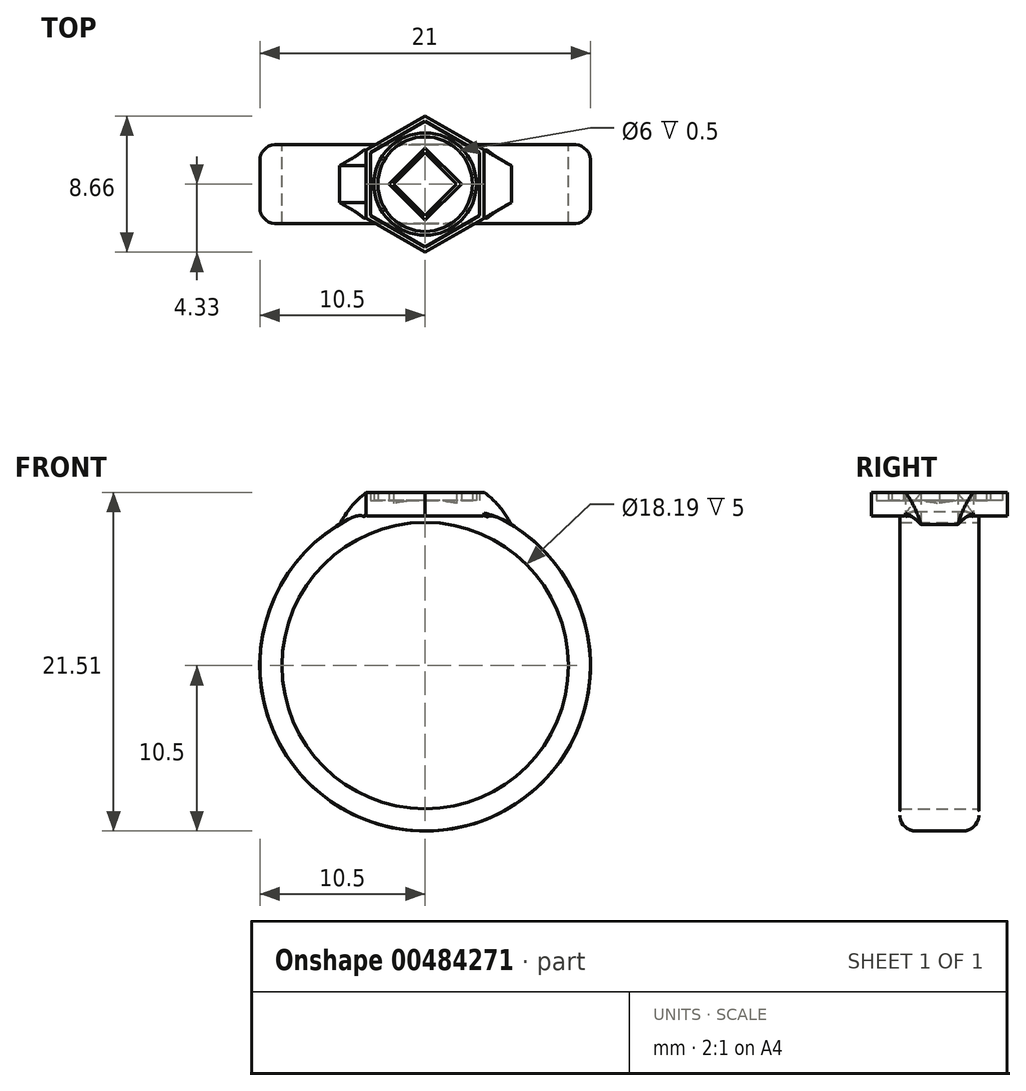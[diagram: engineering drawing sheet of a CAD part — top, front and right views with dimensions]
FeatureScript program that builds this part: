
annotation { "Feature Type Name" : "Feature", "Feature Type Description" : "" }
export const myFeature = defineFeature(function(context is Context, id is Id, definition is map)
    precondition{}
    {
        {
            var Q0;
            Q0=qCreatedBy(makeId("Front.planeOp"),FACE);
            var sketch = newSketch(context, id + "F0", { "sketchPlane" : qUnion([Q0])});
            skCircle(sketch, "E0", {"center": v(0, 0) * mm, "radius": 9.1 * mm});
            skCircle(sketch, "E1", {"center": v(0, 0) * mm, "radius": 10.5 * mm});
            skSolve(sketch);
        }
        {
            var Q0;
            Q0=makeQuery(id+"F0.imprint","IMPRINT",FACE,{"disambiguationData":[TD([[makeQuery(id+"F0.imprint","IMPRINT",EDGE,{"derivedFrom":sQuery(id+"F0.wireOp",EDGE,"E0")}),-1.0]])]});
            extrude(context, id + "F1", {"entities" : qUnion([Q0]), "endBound" : BoundingType.SYMMETRIC, "depth" : 5 * mm});
        }
        {
            var Q0;
            Q0=qCreatedBy(makeId("Top.planeOp"),FACE);
            var sketch = newSketch(context, id + "F2", { "sketchPlane" : qUnion([Q0])});
            skLineSegment(sketch, "E2.0", {"start": v(0, 4) * mm, "end": v(3.46, 2) * mm});
            skLineSegment(sketch, "E2.1", {"start": v(3.46, 2) * mm, "end": v(3.46, -2) * mm});
            skLineSegment(sketch, "E2.2", {"start": v(3.46, -2) * mm, "end": v(0, -4) * mm});
            skLineSegment(sketch, "E2.3", {"start": v(0, -4) * mm, "end": v(-3.46, -2) * mm});
            skLineSegment(sketch, "E2.4", {"start": v(-3.46, -2) * mm, "end": v(-3.46, 2) * mm});
            skLineSegment(sketch, "E2.5", {"start": v(-3.46, 2) * mm, "end": v(0, 4) * mm});
            skCircle(sketch, "E3", {"center": v(0, 0) * mm, "radius": 3.25 * mm});
            skCircle(sketch, "E4.cCircle", {"center": v(0, 0) * mm, "radius": 3.25 * mm, "construction": true});
            skLineSegment(sketch, "E5.0", {"start": v(0, 2.3) * mm, "end": v(2.3, 0) * mm});
            skLineSegment(sketch, "E5.1", {"start": v(2.3, 0) * mm, "end": v(0, -2.3) * mm});
            skLineSegment(sketch, "E5.2", {"start": v(0, -2.3) * mm, "end": v(-2.3, 0) * mm});
            skLineSegment(sketch, "E5.3", {"start": v(-2.3, 0) * mm, "end": v(0, 2.3) * mm});
            skCircle(sketch, "E6", {"center": v(0, 0) * mm, "radius": 3 * mm});
            skPoint(sketch, "E7.cCircle.perimeterSnap0", {"position": v(3.46, 0) * mm});
            skLineSegment(sketch, "E7.0", {"start": v(3.75, 2.17) * mm, "end": v(3.75, -2.17) * mm});
            skLineSegment(sketch, "E7.1", {"start": v(3.75, -2.17) * mm, "end": v(0, -4.33) * mm});
            skLineSegment(sketch, "E7.2", {"start": v(0, -4.33) * mm, "end": v(-3.75, -2.17) * mm});
            skLineSegment(sketch, "E7.3", {"start": v(-3.75, -2.17) * mm, "end": v(-3.75, 2.17) * mm});
            skLineSegment(sketch, "E7.4", {"start": v(-3.75, 2.17) * mm, "end": v(0, 4.33) * mm});
            skLineSegment(sketch, "E7.5", {"start": v(0, 4.33) * mm, "end": v(3.75, 2.17) * mm});
            skPoint(sketch, "E7.0.midPoint", {"position": v(3.75, 0) * mm});
            skPoint(sketch, "E7.0.midPoint.positionSnap0", {"position": v(3.46, 0) * mm});
            skLineSegment(sketch, "E8.0", {"start": v(-2, 0) * mm, "end": v(0, 2) * mm});
            skLineSegment(sketch, "E8.1", {"start": v(0, 2) * mm, "end": v(2, 0) * mm});
            skLineSegment(sketch, "E8.2", {"start": v(2, 0) * mm, "end": v(0, -2) * mm});
            skLineSegment(sketch, "E8.3", {"start": v(0, -2) * mm, "end": v(-2, 0) * mm});
            skSolve(sketch);
        }
        {
            var Q0;
            Q0=makeQuery(id+"F2.imprint","IMPRINT",FACE,{"disambiguationData":[TD([[makeQuery(id+"F2.imprint","IMPRINT",EDGE,{"derivedFrom":sQuery(id+"F2.wireOp",EDGE,"E5.0")}),-1.0]])]});
            var Q1;
            Q1=makeQuery(id+"F2.imprint","IMPRINT",FACE,{"disambiguationData":[TD([[makeQuery(id+"F2.imprint","IMPRINT",EDGE,{"derivedFrom":sQuery(id+"F2.wireOp",EDGE,"E5.0")}),1.0]])]});
            var Q2;
            Q2=makeQuery(id+"F2.imprint","IMPRINT",FACE,{"disambiguationData":[TD([[makeQuery(id+"F2.imprint","IMPRINT",EDGE,{"derivedFrom":sQuery(id+"F2.wireOp",EDGE,"E3")}),1.0]])]});
            var Q3;
            Q3=makeQuery(id+"F2.imprint","IMPRINT",FACE,{"disambiguationData":[TD([[makeQuery(id+"F2.imprint","IMPRINT",EDGE,{"derivedFrom":sQuery(id+"F2.wireOp",EDGE,"E2.0")}),-1.0]])]});
            var Q4;
            Q4=makeQuery(id+"F2.imprint","IMPRINT",FACE,{"disambiguationData":[TD([[makeQuery(id+"F2.imprint","IMPRINT",EDGE,{"derivedFrom":sQuery(id+"F2.wireOp",EDGE,"E2.0")}),1.0]])]});
            extrude(context, id + "F3", {"entities" : qUnion([Q0, Q1, Q2, Q3, Q4]), "operationType" : NewBodyOperationType.ADD, "depth" : 11 * mm, "hasSecondDirection" : true, "secondDirectionOppositeDirection" : false, "secondDirectionDepth" : 9.5 * mm});
        }
        {
            var Q0;
            Q0=makeQuery(id+"F1.opExtrude","CAP_EDGE",EDGE,{"disambiguationData":[OSD([sQuery(id+"F0.wireOp",EDGE,"E1")])],"isStart":true});
            var Q1;
            Q1=makeQuery(id+"F1.opExtrude","CAP_EDGE",EDGE,{"disambiguationData":[OSD([sQuery(id+"F0.wireOp",EDGE,"E1")])],"isStart":false});
            fillet(context, id + "F4", {"entities" : qUnion([Q0, Q1]), "radius" : 1 * mm, "tangentPropagation" : true, "allowEdgeOverflow" : false});
        }
        {
            var Q0;
            Q0=makeQuery(id+"F2.imprint","IMPRINT",FACE,{"disambiguationData":[TD([[makeQuery(id+"F2.imprint","IMPRINT",EDGE,{"derivedFrom":sQuery(id+"F2.wireOp",EDGE,"E5.0")}),1.0]])]});
            var Q1;
            Q1=makeQuery(id+"F2.imprint","IMPRINT",FACE,{"disambiguationData":[TD([[makeQuery(id+"F2.imprint","IMPRINT",EDGE,{"derivedFrom":sQuery(id+"F2.wireOp",EDGE,"E2.0")}),-1.0]])]});
            extrude(context, id + "F5", {"entities" : qUnion([Q0, Q1]), "operationType" : NewBodyOperationType.REMOVE, "depth" : 11 * mm, "hasSecondDirection" : true, "secondDirectionOppositeDirection" : false, "secondDirectionDepth" : 10.5 * mm});
        }
        {
            var Q0;
            Q0=qCreatedBy(makeId("Front.planeOp"),FACE);
            var sketch = newSketch(context, id + "F6", { "sketchPlane" : qUnion([Q0])});
            skCircle(sketch, "E9", {"center": v(0.02, 6.14) * mm, "radius": 6.14 * mm});
            skPoint(sketch, "E9.first.point", {"position": v(0, 0) * mm});
            skPoint(sketch, "E9.second.point", {"position": v(-3.77, 10.99) * mm});
            skPoint(sketch, "E9.third.point", {"position": v(-5.85, 4.33) * mm});
            skCircle(sketch, "E10", {"center": v(0, 0) * mm, "radius": 9.64 * mm});
            skLineSegment(sketch, "E11", {"start": v(3.75, 11.02) * mm, "end": v(3.75, 8.88) * mm});
            skLineSegment(sketch, "E12", {"start": v(-3.77, 10.99) * mm, "end": v(-3.77, 8.87) * mm});
            skSolve(sketch);
        }
        {
            var Q0;
            {var subQ0=sQuery(id+"F6.wireOp",EDGE,"E11");Q0=makeQuery(id+"F6.imprint","IMPRINT",FACE,{"disambiguationData":[TD([[makeQuery(id+"F6.imprint","IMPRINT",EDGE,{"derivedFrom":subQ0}),1.0]])]});}
            var Q1;
            {var subQ0=sQuery(id+"F6.wireOp",EDGE,"E12");Q1=makeQuery(id+"F6.imprint","IMPRINT",FACE,{"disambiguationData":[TD([[makeQuery(id+"F6.imprint","IMPRINT",EDGE,{"derivedFrom":subQ0}),-1.0]])]});}
            extrude(context, id + "F7", {"entities" : qUnion([Q0, Q1]), "operationType" : NewBodyOperationType.ADD, "endBound" : BoundingType.SYMMETRIC, "depth" : 4.34 * mm});
        }
        {
            var Q0;
            {var subQ0=sQuery(id+"F6.wireOp",EDGE,"E9");Q0=makeQuery(id+"F7.opExtrude","CAP_EDGE",EDGE,{"disambiguationData":[OSD([subQ0]),TDD([makeQuery(id+"F6.imprint","IMPRINT",EDGE,{"disambiguationData":[TD([[makeQuery(id+"F6.imprint","INTERSECT",VERTEX,{"derivedFrom":[subQ0,sQuery(id+"F6.wireOp",EDGE,"E11")]}),1.0]])],"derivedFrom":subQ0})])],"isStart":false});}
            var Q1;
            {var subQ0=sQuery(id+"F6.wireOp",EDGE,"E9");Q1=makeQuery(id+"F7.opExtrude","CAP_EDGE",EDGE,{"disambiguationData":[OSD([subQ0]),TDD([makeQuery(id+"F6.imprint","IMPRINT",EDGE,{"disambiguationData":[TD([[makeQuery(id+"F6.imprint","INTERSECT",VERTEX,{"derivedFrom":[subQ0,sQuery(id+"F6.wireOp",EDGE,"E11")]}),1.0]])],"derivedFrom":subQ0})])],"isStart":true});}
            var Q2;
            {var subQ0=sQuery(id+"F6.wireOp",EDGE,"E9");Q2=makeQuery(id+"F7.opExtrude","CAP_EDGE",EDGE,{"disambiguationData":[OSD([subQ0]),TDD([makeQuery(id+"F6.imprint","IMPRINT",EDGE,{"disambiguationData":[TD([[makeQuery(id+"F6.imprint","INTERSECT",VERTEX,{"derivedFrom":[subQ0,sQuery(id+"F6.wireOp",EDGE,"E12")]}),-1.0]])],"derivedFrom":subQ0})])],"isStart":false});}
            var Q3;
            {var subQ0=sQuery(id+"F6.wireOp",EDGE,"E9");Q3=makeQuery(id+"F7.opExtrude","CAP_EDGE",EDGE,{"disambiguationData":[OSD([subQ0]),TDD([makeQuery(id+"F6.imprint","IMPRINT",EDGE,{"disambiguationData":[TD([[makeQuery(id+"F6.imprint","INTERSECT",VERTEX,{"derivedFrom":[subQ0,sQuery(id+"F6.wireOp",EDGE,"E12")]}),-1.0]])],"derivedFrom":subQ0})])],"isStart":true});}
            chamfer(context, id + "F8", {"entities" : qUnion([Q0, Q1, Q2, Q3]), "width" : 1 * mm, "tangentPropagation" : true});
        }
    });
